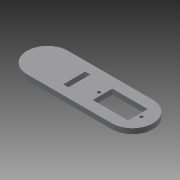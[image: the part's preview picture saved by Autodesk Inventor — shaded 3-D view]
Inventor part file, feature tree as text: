
AUTODESK INVENTOR PART (.ipt)
format: ipt  version: 2013 (Build 170138000, 138)  size: 107,520 bytes
history: native  units: mm
features: other x3, extrude x1, sketch x1
ambient origin geometry x8: Origin, YZ Plane, XZ Plane, XY Plane, X Axis, Y Axis, Z Axis, Center Point
feature tree (5):
  other  "Blocks"
  extrude  "Extrusion5"  Depth=3.0mm
  sketch  "Sketch1"  dims[d0=3.0mm d2=3.0mm d3=0.1mm d7=22.5mm d8=12.4mm d9=4.5mm d10=4.5mm d11=2.0mm d12=2.0mm d23=80.0mm d24=26.0mm d25=5.0mm d29=3.25mm d30=14.0mm d31=30.0mm d38=13.0mm d39=13.0mm d40=3.25mm d41=0.0mm]
  other  "Block1"
  other  "Block1:1"
